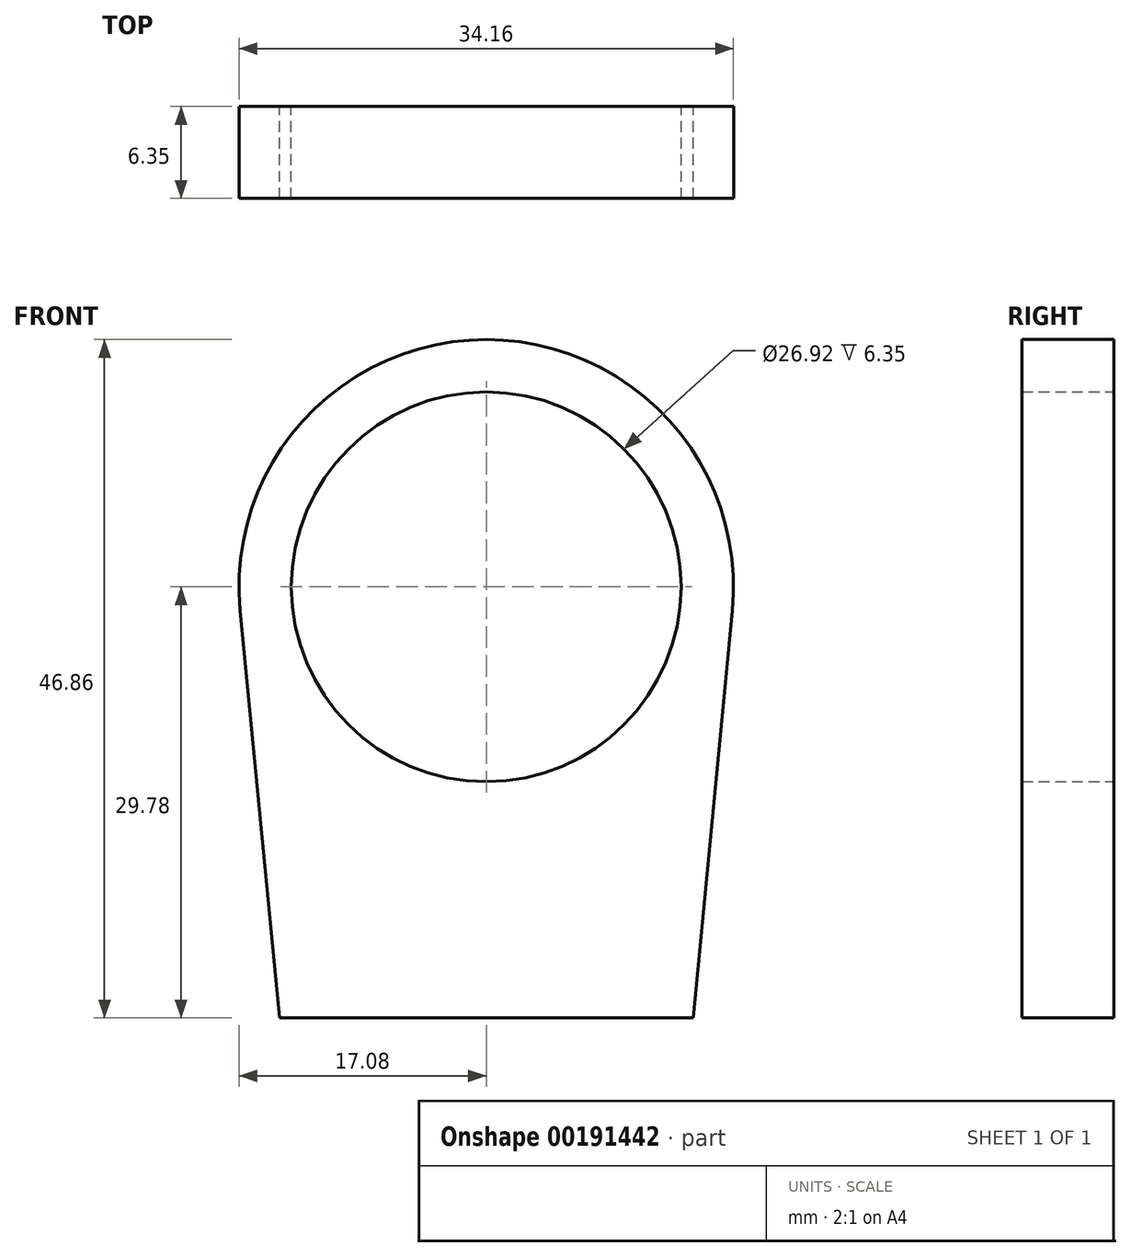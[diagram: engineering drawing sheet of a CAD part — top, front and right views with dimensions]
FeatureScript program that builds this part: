
annotation { "Feature Type Name" : "Feature", "Feature Type Description" : "" }
export const myFeature = defineFeature(function(context is Context, id is Id, definition is map)
    precondition{}
    {
        {
            var Q0;
            Q0=qCreatedBy(makeId("Front.planeOp"),FACE);
            var sketch = newSketch(context, id + "F0", { "sketchPlane" : qUnion([Q0])});
            skArc(sketch, "E0", {"start": v(17, -1.64) * mm, "mid": v(0, 17.08) * mm, "end": v(-17, -1.64) * mm});
            skLineSegment(sketch, "E1", {"start": v(-14.29, -29.78) * mm, "end": v(14.29, -29.78) * mm});
            skLineSegment(sketch, "E2", {"start": v(-14.29, -29.78) * mm, "end": v(-17.16, 0) * mm});
            skLineSegment(sketch, "E3", {"start": v(14.29, -29.78) * mm, "end": v(17.16, 0) * mm});
            skCircle(sketch, "E4", {"center": v(0, 0) * mm, "radius": 13.46 * mm});
            skSolve(sketch);
        }
        {
            var Q0;
            Q0 = qSketchRegion(id + "F0", true);
            extrude(context, id + "F1", {"entities" : qUnion([Q0]), "depth" : 6.35 * mm});
        }
    });
